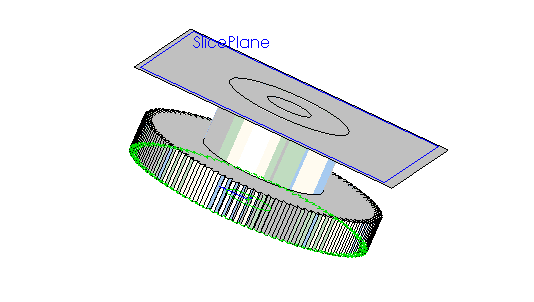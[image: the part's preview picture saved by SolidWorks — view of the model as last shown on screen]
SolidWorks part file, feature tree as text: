
SOLIDWORKS PART (.sldprt)
format: sldprt  version: not decoded by parser v0  size: 750,080 bytes
history: native  units: mm
features: sketch x4, extrude x2, cut_extrude x1, plane x1 (+11 scaffold rows collapsed)
feature tree (19):
  scaffold x11  (default folders/planes/origin — collapsed)
  sketch  "Sketch1"  dims[D1=21.844mm D2=4.064mm]
  extrude  "Extrude1"  Depth=3.175mm
  sketch  "Sketch2"  dims[D1=11.049mm]
  extrude  "Extrude2"  Depth=5.715mm
  sketch  "Sketch3"  dims[D1=20.4724mm]
  cut_extrude  "Cut-Extrude1"  [1 undecoded]
  plane  "SlicePlane"  Offset=8.763mm
  sketch  "Sketch5"
decode coverage: 5 of 7 modeling features carry decoded parameters
note: 1 parameter value undecoded
note: suppression state not decoded; provenance and decode notes live in map.json
